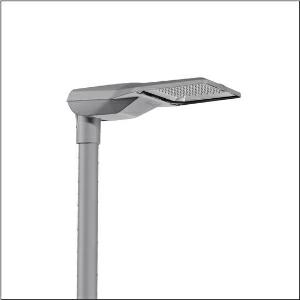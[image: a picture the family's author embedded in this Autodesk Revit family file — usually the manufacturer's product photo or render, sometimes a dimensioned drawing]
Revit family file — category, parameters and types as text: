
# Revit family: streetlight_sl_21_midi___pl52_5xe7h33a08lb_72c3
name_source: partatom
category: Lighting Fixtures
units: mm (PartAtom-declared; Revit-internal decimal feet)

## family parameters
Cut with Voids When Loaded = No
Host = Face
Light Source = No
Part Type = Normal
Room Calculation Point = No
Round Connector Dimension = Use Diameter
Shared = No

## types (1)
- --- (1 x LED, 14100 lm, 98.3 W, 3000K)
    Apparent Load = 98 VA
    CIE Flux Codes = 27 59 98 100 100
    Color Rendering = 70
    Color Temperature = 3000K
    Default Elevation = 1800 mm
    Description = Streetlight SL 21 midi, mast luminaire, primary light control with lens, of PMMA, primary optical cover: cover, of toughened safety glass, transparent, light distribution: PL52, light emission: direct distribution, primary light characteristic: asymmetric, installation type: post-top, side-entry, LED, 3G 1.5mm², High Power LED, rated luminous flux: 14.100lm, luminous efficacy: 143lm/W, light colour: 730, colour temperature: 3000K, control: overheat protection, constant luminous flux control, time-dependent luminous flux control, flexible luminous flux parameterisation, mains connection: 220..240V, AC, 50/60Hz, connection cable pre-assembled, cable length: 10,5m, wiring characteristics: H07RN-F, start of lifetime: 98W, end of service life: 101W, reduction: 44W, luminaire housing, of diecast aluminium, powder-coated, Siteco® metallic grey (DB 702S), corrosivity category C5 mid according to DIN EN ISO 12944, please order mast flange separately, inclination adjustable: 0°, 5°, 10°, 15°, sealing non-destructively replaceable, multi-level sealing system, length: 644mm, width: 335mm, height: 110mm, mast flange for spigot size: 42mm (side-entry): 5XC10008XM4, 60/48mm (side-entry/post-top): 5XC10108XM2, 76/60mm (side-entry/post-top): 5XC10108XM1, protection rating (complete): IP66, insulation class (complete): insulation class II (safety insulation), certification: CE, ENEC, ENEC+, VDE, impact resistance: IK09, permissible operating ambient temperature for outdoor applications: -40..+50°C, standard-compliant lighting for roads and squares, packaging unit: 1 piece

Light Distribution: PL52
    Height = 111 mm
    Lamp = 1 x LED
    Lamp Light Flux = 14100 lm
    Lamp Power = 98.3 W
    Lamp count = 1
    Length = 644 mm
    Luminous efficacy = 143 lm/W
    Manufacturer = Siteco
    ModVariant = No
    Model = 5XE7H33A08LB
    Number of Poles = 1
    OnlyDefault = Yes
    Power Factor = 1
    Product Name = Streetlight SL 21 midi | PL52
    Product group = mast luminaire | pylon top
    ProductGroupID = 6100
    Protection Class = Protection class II
    Protection Degree = IP 66
    RLX_Detail_Level = 1
    RLX_Emergency_Light_Flux = 0 lm
    RLX_Emergency_Type = 0
    RLX_Emergency_Type_DB = No
    RlxData = <blob elided: 100529 chars, md5=e78de671>
    Socket = socket
    Standby Power = 0 W
    System Light Flux = 14100 lm
    System Power = 98 W
    Type Comments = factory setting: luminous flux: 100 % | Output Level: 100 % | 1020 mA
    Type Image = l_1004298.jpg
    URL = http://relux.com
    VarID = @adj_142835
    Voltage = 0 V
    Weight = 0.00 kg
    Width = 336 mm

## geometry (parser evidence)
native form markers: Blend x4, Sweep x10
no freeform markers — native parametric forms only
